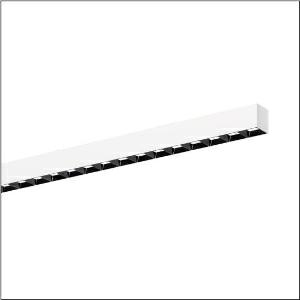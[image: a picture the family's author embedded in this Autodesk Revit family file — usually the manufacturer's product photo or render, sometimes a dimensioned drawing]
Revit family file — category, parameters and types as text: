
# Revit family: silica_r__21_51mx22da34wb_da43
name_source: partatom
category: Lighting Fixtures
units: mm (PartAtom-declared; Revit-internal decimal feet)

## family parameters
Cut with Voids When Loaded = No
Host = Face
Light Source = No
Part Type = Normal
Room Calculation Point = No
Round Connector Dimension = Use Diameter
Shared = No

## types (1)
- --- (1 x LED, 4320 lm, 27.4 W, 3000K)
    Apparent Load = 27 VA
    CIE Flux Codes = 86 100 100 100 100
    Color Rendering = 80
    Color Temperature = 3000K
    Default Elevation = 1800 mm
    Description = Silica® 21, office luminaire, primary light control with darklight reflector, of PMMA, black, CAT 2 (L<= 3000cd/m²), light emission: direct distribution, primary light characteristic: symmetric, installation type: surface-mounted, LED, rated luminous flux: 4.320lm, luminous efficacy: 158lm/W, light colour: 830, colour temperature: 3000K, with terminal, 3+2-pole, max. 2.5mm², mains connection: 220..240V, AC, 50/60Hz, rated input power: 27.4W, luminaire housing, of aluminium, traffic white (RAL 9016), length: 1.204mm, width: 53mm, height: 53mm, protection rating (complete): IP20, insulation class (complete): insulation class I (protective earthing), certification: CE, permissible operating ambient temperature: 0..+35°C, standard: EN 50419, packaging unit: 1 piece
    Height = 0 mm  [stored 0 ft]
    Lamp = 1 x LED
    Lamp Light Flux = 4320 lm
    Lamp Power = 27.4 W
    Lamp count = 1
    Length = 1204 mm
    Luminous efficacy = 158 lm/W
    Manufacturer = Siteco
    ModVariant = No
    Model = 51MX22DA34WB
    Mounting Place = Ceiling
    Mounting Type = Recessed
    Number of Poles = 1
    OnlyDefault = Yes
    Power Factor = 1
    Product Name = Silica® 21
    Product group = office luminaire | ceiling recessed
    ProductGroupID = 401
    Protection Class = Protection class I
    Protection Degree = IP 20
    RLX_Detail_Level = 1
    RLX_Emergency_Light_Flux = 0 lm
    RLX_Emergency_Type = 0
    RLX_Emergency_Type_DB = No
    RlxData = <blob elided: 41225 chars, md5=4b06fb0c>
    Socket = socket
    Standby Power = 0 W
    System Light Flux = 4320 lm
    System Power = 27 W
    Type Comments = factory setting: luminous flux: 100 % | dim-lin: 254 | 392 mA
    Type Image = l_1313592.jpg
    URL = http://relux.com
    VarID = @adj_074617
    Voltage = 0 V
    Weight = 0.00 kg
    Width = 53 mm

note: [stored X ft] marks values corroborated as IEEE doubles in the binary element streams (Revit-internal decimal feet)

## geometry (parser evidence)
native form markers: Blend x4, Sweep x10
no freeform markers — native parametric forms only
